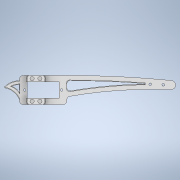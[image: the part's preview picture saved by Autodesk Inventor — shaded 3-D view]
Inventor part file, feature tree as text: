
AUTODESK INVENTOR PART (.ipt)
format: ipt  version: 2020.3 (Build 243373000, 373)  size: 335,360 bytes
history: native  units: mm
features: fillet x7, hole x3, sketch x2, extrude x2, chamfer x1
ambient origin geometry x8: Origin, YZ Plane, XZ Plane, XY Plane, X Axis, Y Axis, Z Axis, Center Point
bodies: Solid1 (feature_tree)
feature tree (15):
  sketch  "Sketch1"  dims[d4=6.0mm d5=24.6mm d6=12.4mm d7=5.0mm d15=7.0mm]
  extrude  "Extrusion1"  Depth=24.6mm
  fillet  "Fillet1"  Radius=12.4mm
  fillet  "Fillet2"  Radius=5.0mm
  fillet  "Fillet3"  Radius=7.0mm
  hole  "Hole1"  [1 undecoded]
  fillet  "Fillet4"  Radius=20.0mm
  hole  "Hole2"  [1 undecoded]
  extrude  "Extrusion3"  Depth=0.5mm
  sketch  "Sketch3"  dims[d17=6.0mm d18=4.0mm d21=20.0mm d23=80.0mm d24=15.0mm d29=29.670597mm d30=6.0mm d31=10.0mm d33=6.0mm d34=0.0mm d40=3.0mm d41=3.0mm d42=2.0mm d43=4.0mm d44=3.0mm d45=4.0mm d50=13.0mm d51=12.0mm d52=22.68928mm d53=16.057029mm d54=2.0mm d55=50.8mm d56=4.0mm d57=2.0mm d58=90.0deg d59=8.0mm d60=20.594885mm d61=0.5mm d62=2.1mm d63=4.0mm d64=4.0mm d65=2.0mm d66=90.0deg d67=8.0mm d68=20.594885mm d69=20.92mm d70=0.0mm d71=2.0mm d80=2.0mm d81=2.0mm d82=45.0deg d87=0.5mm d88=0.5mm d89=6.8mm d90=28.4mm d91=6.0mm d99=3.3mm d100=6.0mm d101=4.0mm d102=2.0mm d103=90.0deg d104=4.3mm d105=0.0mm]
  hole  "Hole5"  [1 undecoded]
  fillet  "Fillet5"  Radius=6.0mm
  chamfer  "Chamfer2"  Distance=10.0mm
  fillet  "Fillet8"  Radius=6.0mm
  fillet  "Fillet9"  Radius=3.0mm
note: 3 required parameter values undecoded (feature->parameter linkage not recoverable at this tier; creation-order binding heuristic only, values carry confidence <= 0.55)
